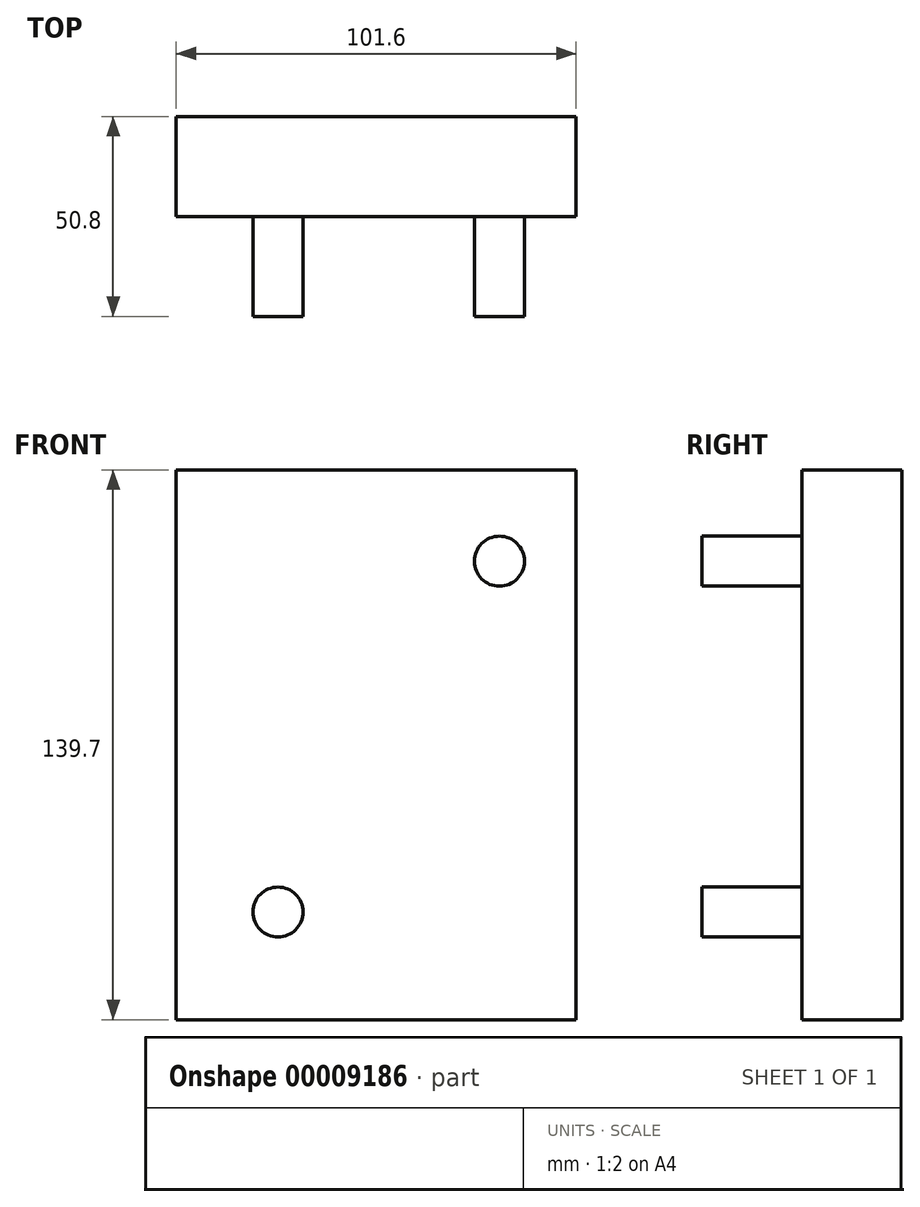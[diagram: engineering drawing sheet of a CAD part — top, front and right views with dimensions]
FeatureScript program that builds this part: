
annotation { "Feature Type Name" : "Feature", "Feature Type Description" : "" }
export const myFeature = defineFeature(function(context is Context, id is Id, definition is map)
    precondition{}
    {
        {
            var Q0;
            Q0=qCreatedBy(makeId("Front.planeOp"),FACE);
            var sketch = newSketch(context, id + "F0", { "sketchPlane" : qUnion([Q0])});
            skLineSegment(sketch, "E0.rect.bottom", {"start": v(-50.8, 69.85) * mm, "end": v(50.8, 69.85) * mm});
            skLineSegment(sketch, "E0.rect.top", {"start": v(-50.8, -69.85) * mm, "end": v(50.8, -69.85) * mm});
            skLineSegment(sketch, "E0.rect.left", {"start": v(-50.8, 69.85) * mm, "end": v(-50.8, -69.85) * mm});
            skLineSegment(sketch, "E0.rect.right", {"start": v(50.8, 69.85) * mm, "end": v(50.8, -69.85) * mm});
            skPoint(sketch, "E0.rect.middle", {"position": v(0, 0) * mm});
            skSolve(sketch);
        }
        {
            var Q0;
            Q0=makeQuery(id+"F0.imprint","IMPRINT",FACE,{"disambiguationData":[TD([[makeQuery(id+"F0.imprint","IMPRINT",EDGE,{"derivedFrom":sQuery(id+"F0.wireOp",EDGE,"E0.rect.bottom")}),-1.0]])]});
            extrude(context, id + "F1", {"entities" : qUnion([Q0]), "depth" : 25.4 * mm});
        }
        {
            var Q0;
            Q0=makeQuery(id+"F1.opExtrude","CAP_FACE",FACE,{"disambiguationData":[OSD([sQuery(id+"F0.wireOp",EDGE,"E0.rect.bottom"),sQuery(id+"F0.wireOp",EDGE,"E0.rect.top"),sQuery(id+"F0.wireOp",EDGE,"E0.rect.left"),sQuery(id+"F0.wireOp",EDGE,"E0.rect.right")])],"isStart":false});
            var sketch = newSketch(context, id + "F2", { "sketchPlane" : qUnion([Q0])});
            skCircle(sketch, "E1", {"center": v(31.31, 46.63) * mm, "radius": 6.35 * mm});
            skCircle(sketch, "E2", {"center": v(-24.94, -42.5) * mm, "radius": 6.35 * mm});
            skSolve(sketch);
        }
        {
            var Q0;
            Q0 = qSketchRegion(id + "F2", true);
            extrude(context, id + "F3", {"entities" : qUnion([Q0]), "operationType" : NewBodyOperationType.ADD, "depth" : 25.4 * mm});
        }
    });
